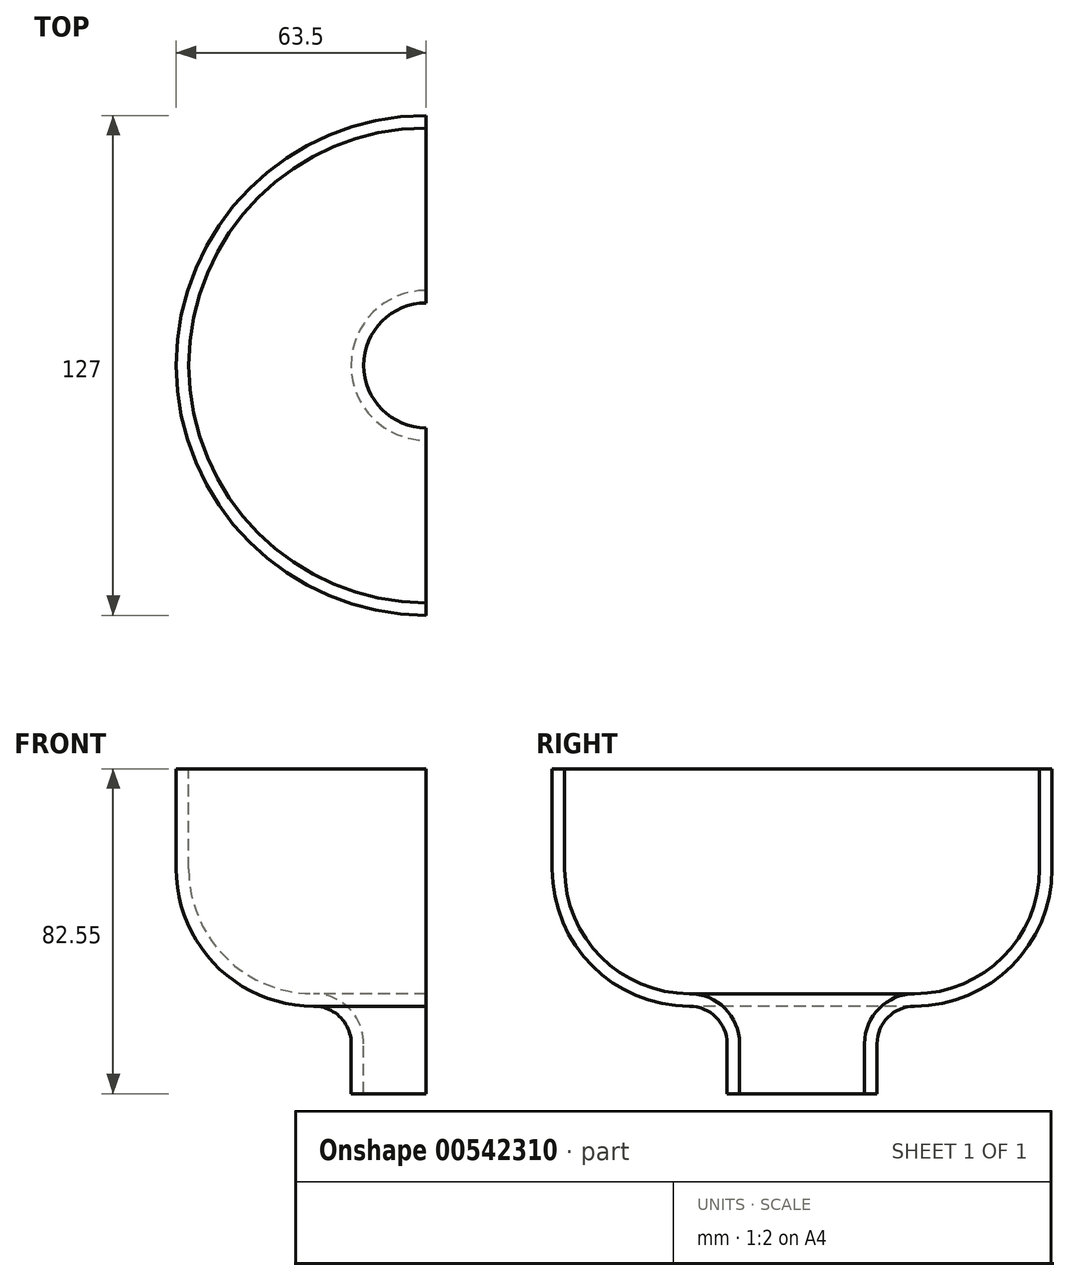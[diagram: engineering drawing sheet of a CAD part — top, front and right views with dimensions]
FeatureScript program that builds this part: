
annotation { "Feature Type Name" : "Feature", "Feature Type Description" : "" }
export const myFeature = defineFeature(function(context is Context, id is Id, definition is map)
    precondition{}
    {
        {
            var Q0;
            Q0=qCreatedBy(makeId("Right.planeOp"),FACE);
            var sketch = newSketch(context, id + "F0", { "sketchPlane" : qUnion([Q0])});
            skLineSegment(sketch, "E0", {"start": v(-60.33, 19.05) * mm, "end": v(-60.32, -6.35) * mm});
            skLineSegment(sketch, "E1", {"start": v(-28.57, -38.1) * mm, "end": v(-28.57, -38.1) * mm});
            skLineSegment(sketch, "E2", {"start": v(-15.87, -50.8) * mm, "end": v(-15.87, -63.5) * mm});
            skPoint(sketch, "E3.visualSharp", {"position": v(-60.32, -38.1) * mm});
            skArc(sketch, "E3.filletArc", {"start": v(-60.33, -6.35) * mm, "mid": v(-51.03, -28.8) * mm, "end": v(-28.57, -38.1) * mm});
            skPoint(sketch, "E4.visualSharp", {"position": v(-15.87, -38.1) * mm});
            skArc(sketch, "E4.filletArc", {"start": v(-15.87, -50.8) * mm, "mid": v(-19.6, -41.82) * mm, "end": v(-28.57, -38.1) * mm});
            skLineSegment(sketch, "E5", {"start": v(0, 39.18) * mm, "end": v(0, -74.76) * mm});
            skLineSegment(sketch, "E6.0", {"start": v(-19.05, -50.8) * mm, "end": v(-19.05, -63.5) * mm});
            skArc(sketch, "E6.1", {"start": v(-19.05, -50.8) * mm, "mid": v(-21.84, -44.06) * mm, "end": v(-28.57, -41.27) * mm});
            skArc(sketch, "E6.2", {"start": v(-63.5, -6.35) * mm, "mid": v(-53.27, -31.05) * mm, "end": v(-28.57, -41.27) * mm});
            skLineSegment(sketch, "E6.3", {"start": v(-63.5, 19.05) * mm, "end": v(-63.5, -6.35) * mm});
            skLineSegment(sketch, "E7", {"start": v(-76.37, 19.05) * mm, "end": v(-60.33, 19.05) * mm});
            skLineSegment(sketch, "E8", {"start": v(-19.05, -63.5) * mm, "end": v(-15.87, -63.5) * mm});
            skSolve(sketch);
        }
        {
            var Q0;
            {var subQ0=sQuery(id+"F0.wireOp",EDGE,"E0");Q0=makeQuery(id+"F0.imprint","IMPRINT",FACE,{"disambiguationData":[TD([[makeQuery(id+"F0.imprint","IMPRINT",EDGE,{"derivedFrom":subQ0}),-1.0]])]});}
            var Q1;
            Q1=sQuery(id+"F0.wireOp",EDGE,"E5");
            revolve(context, id + "F1", {"entities" : qUnion([Q0]), "axis" : qUnion([Q1]), "revolveType" : RevolveType.ONE_DIRECTION, "angle" : 180 * degree});
        }
    });
